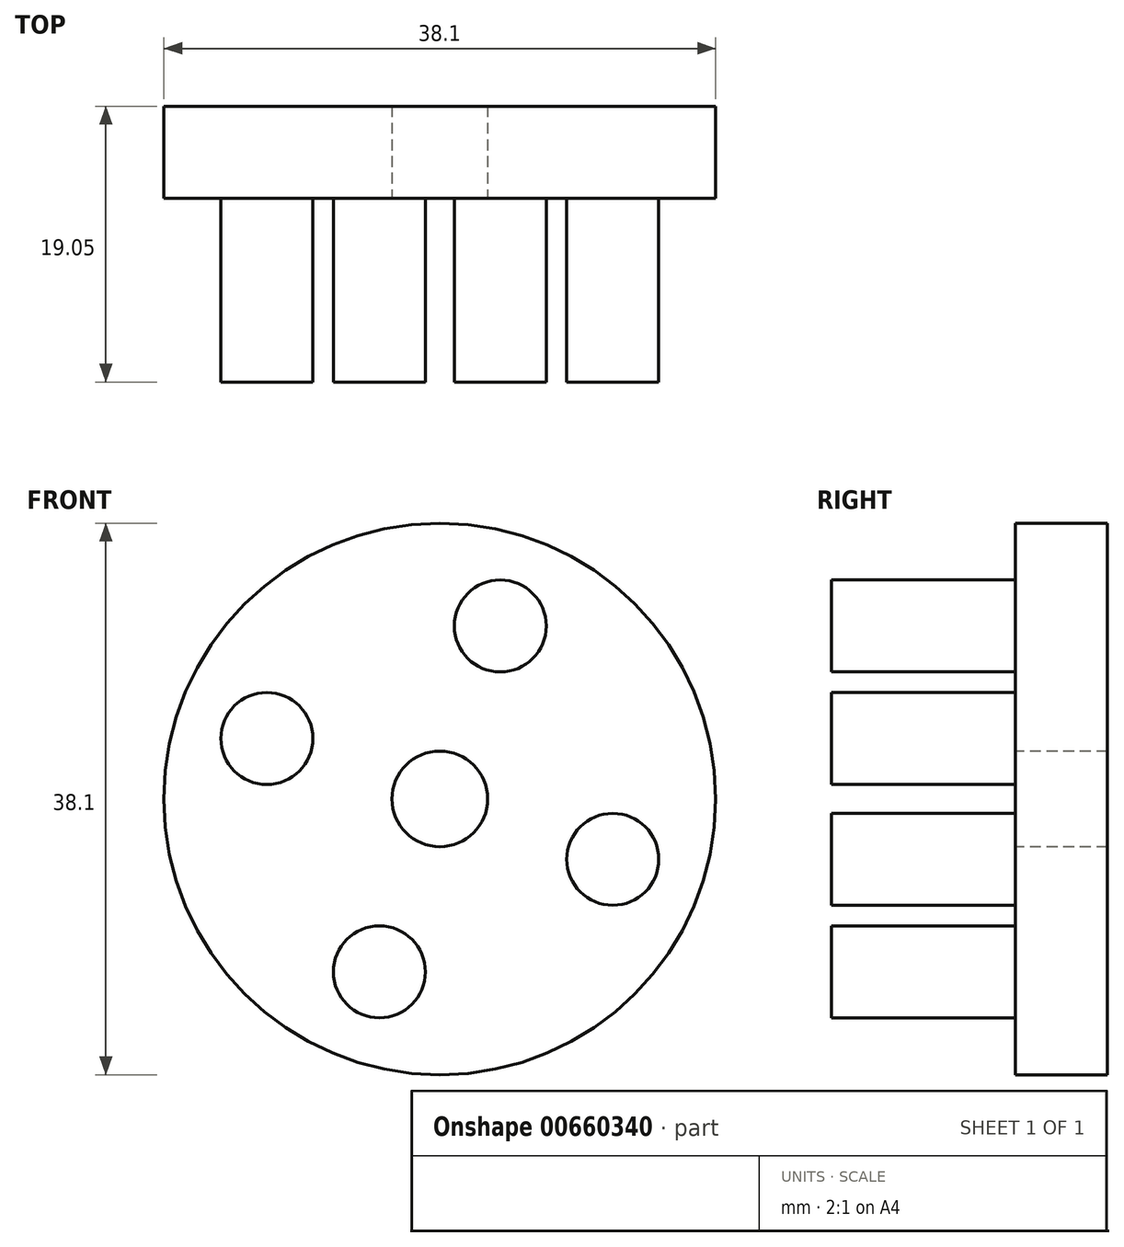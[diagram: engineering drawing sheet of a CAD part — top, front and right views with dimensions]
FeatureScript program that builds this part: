
annotation { "Feature Type Name" : "Feature", "Feature Type Description" : "" }
export const myFeature = defineFeature(function(context is Context, id is Id, definition is map)
    precondition{}
    {
        {
            var Q0;
            Q0=qCreatedBy(makeId("Front.planeOp"),FACE);
            var sketch = newSketch(context, id + "F0", { "sketchPlane" : qUnion([Q0])});
            skCircle(sketch, "E0", {"center": v(0, 0) * mm, "radius": 19.05 * mm});
            skSolve(sketch);
        }
        {
            var Q0;
            Q0=qCreatedBy(makeId("Front.planeOp"),FACE);
            var sketch = newSketch(context, id + "F1", { "sketchPlane" : qUnion([Q0])});
            skCircle(sketch, "E1", {"center": v(4.17, 11.94) * mm, "radius": 3.18 * mm});
            skCircle(sketch, "E2.1.0", {"center": v(-11.94, 4.17) * mm, "radius": 3.18 * mm});
            skCircle(sketch, "E2.2.0", {"center": v(-4.17, -11.94) * mm, "radius": 3.18 * mm});
            skCircle(sketch, "E2.3.0", {"center": v(11.94, -4.17) * mm, "radius": 3.18 * mm});
            skPoint(sketch, "E2.center", {"position": v(0, 0) * mm});
            skSolve(sketch);
        }
        {
            var Q0;
            Q0 = qSketchRegion(id + "F0", true);
            extrude(context, id + "F2", {"entities" : qUnion([Q0]), "depth" : 6.35 * mm, "offsetDistance" : 25.4 * mm});
        }
        {
            var Q0;
            Q0 = qSketchRegion(id + "F1", true);
            extrude(context, id + "F3", {"entities" : qUnion([Q0]), "operationType" : NewBodyOperationType.ADD, "depth" : 19.05 * mm, "offsetDistance" : 25.4 * mm});
        }
        {
            var Q0;
            Q0=makeQuery(id+"F2.opExtrude","CAP_FACE",FACE,{"disambiguationData":[OSD([sQuery(id+"F0.wireOp",EDGE,"E0")])],"isStart":false});
            var sketch = newSketch(context, id + "F4", { "sketchPlane" : qUnion([Q0])});
            skCircle(sketch, "E3", {"center": v(0, 0) * mm, "radius": 3.3 * mm});
            skSolve(sketch);
        }
        {
            var Q0;
            Q0 = qSketchRegion(id + "F4", true);
            extrude(context, id + "F5", {"entities" : qUnion([Q0]), "operationType" : NewBodyOperationType.REMOVE, "oppositeDirection" : true, "depth" : 25.4 * mm, "offsetDistance" : 25.4 * mm});
        }
    });
